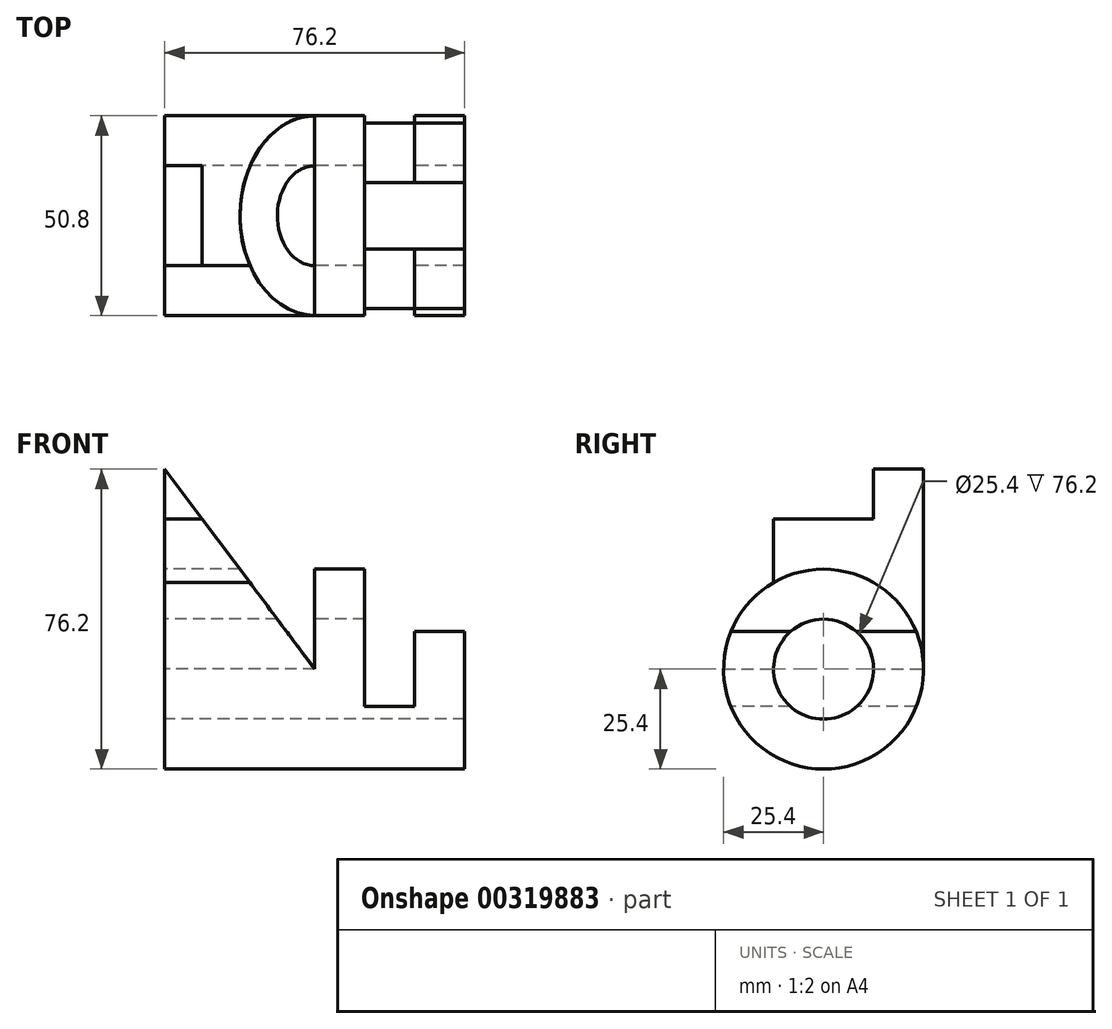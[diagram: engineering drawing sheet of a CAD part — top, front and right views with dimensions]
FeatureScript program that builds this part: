
annotation { "Feature Type Name" : "Feature", "Feature Type Description" : "" }
export const myFeature = defineFeature(function(context is Context, id is Id, definition is map)
    precondition{}
    {
        {
            var Q0;
            Q0=qCreatedBy(makeId("Right.planeOp"),FACE);
            var sketch = newSketch(context, id + "F0", { "sketchPlane" : qUnion([Q0])});
            skCircle(sketch, "E0", {"center": v(0, 0) * mm, "radius": 12.7 * mm});
            skCircle(sketch, "E1", {"center": v(0, 0) * mm, "radius": 25.4 * mm});
            skLineSegment(sketch, "E2", {"start": v(-12.7, 22) * mm, "end": v(-12.7, 38.1) * mm});
            skLineSegment(sketch, "E3", {"start": v(-12.7, 38.1) * mm, "end": v(12.7, 38.1) * mm});
            skLineSegment(sketch, "E4", {"start": v(12.7, 38.1) * mm, "end": v(12.7, 50.8) * mm});
            skLineSegment(sketch, "E5", {"start": v(12.7, 50.8) * mm, "end": v(25.4, 50.8) * mm});
            skLineSegment(sketch, "E6", {"start": v(25.4, 50.8) * mm, "end": v(25.4, 0) * mm});
            skSolve(sketch);
        }
        {
            var Q0;
            Q0=makeQuery(id+"F0.imprint","IMPRINT",FACE,{"disambiguationData":[TD([[makeQuery(id+"F0.imprint","IMPRINT",EDGE,{"derivedFrom":sQuery(id+"F0.wireOp",EDGE,"E0")}),-1.0]])]});
            extrude(context, id + "F1", {"entities" : qUnion([Q0]), "depth" : 76.2 * mm});
        }
        {
            var Q0;
            {var subQ0=sQuery(id+"F0.wireOp",EDGE,"E2");Q0=makeQuery(id+"F0.imprint","IMPRINT",FACE,{"disambiguationData":[TD([[makeQuery(id+"F0.imprint","IMPRINT",EDGE,{"derivedFrom":subQ0}),-1.0]])]});}
            extrude(context, id + "F2", {"entities" : qUnion([Q0]), "depth" : 38.1 * mm});
        }
        {
            var Q0;
            Q0=makeQuery(id+"F1.opExtrude","CAP_FACE",FACE,{"disambiguationData":[OSD([sQuery(id+"F0.wireOp",EDGE,"E0"),sQuery(id+"F0.wireOp",EDGE,"E1")])],"isStart":false});
            var sketch = newSketch(context, id + "F3", { "sketchPlane" : qUnion([Q0])});
            skLineSegment(sketch, "E7", {"start": v(-23.55, 9.53) * mm, "end": v(23.55, 9.53) * mm});
            skSolve(sketch);
        }
        {
            var Q0;
            {var subQ0=sQuery(id+"F3.wireOp",EDGE,"E7");var subQ1=makeQuery(id+"F1.opExtrude","CAP_EDGE",EDGE,{"disambiguationData":[OSD([sQuery(id+"F0.wireOp",EDGE,"E1")])],"isStart":false});var subQ2=makeQuery(id+"F3.imprint","INTERSECT",VERTEX,{"disambiguationData":[OD(0.0)],"derivedFrom":[subQ1,subQ0]});Q0=makeQuery(id+"F3.imprint","IMPRINT",FACE,{"disambiguationData":[TD([[makeQuery(id+"F3.imprint","IMPRINT",EDGE,{"disambiguationData":[TD([[subQ2,-1.0]])],"derivedFrom":subQ0}),1.0]])]});}
            extrude(context, id + "F4", {"entities" : qUnion([Q0]), "operationType" : NewBodyOperationType.REMOVE, "oppositeDirection" : true, "depth" : 25.4 * mm});
        }
        {
            var Q0;
            Q0=makeQuery(id+"F2.opExtrude","SWEPT_FACE",FACE,{"disambiguationData":[OSD([sQuery(id+"F0.wireOp",EDGE,"E6")])]});
            var sketch = newSketch(context, id + "F5", { "sketchPlane" : qUnion([Q0])});
            skLineSegment(sketch, "E8", {"start": v(0, 50.8) * mm, "end": v(-38.1, 0) * mm});
            skLineSegment(sketch, "E9", {"start": v(-38.1, 0) * mm, "end": v(-38.1, 50.8) * mm});
            skLineSegment(sketch, "E10", {"start": v(-38.1, 50.8) * mm, "end": v(0, 50.8) * mm});
            skSolve(sketch);
        }
        {
            var Q0;
            Q0 = qSketchRegion(id + "F5", true);
            extrude(context, id + "F6", {"entities" : qUnion([Q0]), "operationType" : NewBodyOperationType.REMOVE, "endBound" : BoundingType.THROUGH_ALL, "oppositeDirection" : true, "depth" : 25.4 * mm});
        }
        {
            var Q0;
            Q0=qCreatedBy(makeId("Front.planeOp"),FACE);
            var sketch = newSketch(context, id + "F7", { "sketchPlane" : qUnion([Q0])});
            skLineSegment(sketch, "E11.0", {"start": v(50.8, 9.53) * mm, "end": v(50.8, 25.4) * mm});
            skLineSegment(sketch, "E12.bottom", {"start": v(50.8, 25.4) * mm, "end": v(63.5, 25.4) * mm});
            skLineSegment(sketch, "E12.top", {"start": v(50.8, -9.53) * mm, "end": v(63.5, -9.53) * mm});
            skLineSegment(sketch, "E12.left", {"start": v(50.8, 25.4) * mm, "end": v(50.8, -9.53) * mm});
            skLineSegment(sketch, "E12.right", {"start": v(63.5, 25.4) * mm, "end": v(63.5, -9.53) * mm});
            skSolve(sketch);
        }
        {
            var Q0;
            Q0 = qSketchRegion(id + "F7", true);
            extrude(context, id + "F8", {"entities" : qUnion([Q0]), "operationType" : NewBodyOperationType.REMOVE, "endBound" : BoundingType.THROUGH_ALL, "oppositeDirection" : true, "depth" : 25.4 * mm, "hasSecondDirection" : true, "secondDirectionBound" : SecondDirectionBoundingType.THROUGH_ALL, "secondDirectionOppositeDirection" : false, "secondDirectionDepth" : 25.4 * mm});
        }
    });
